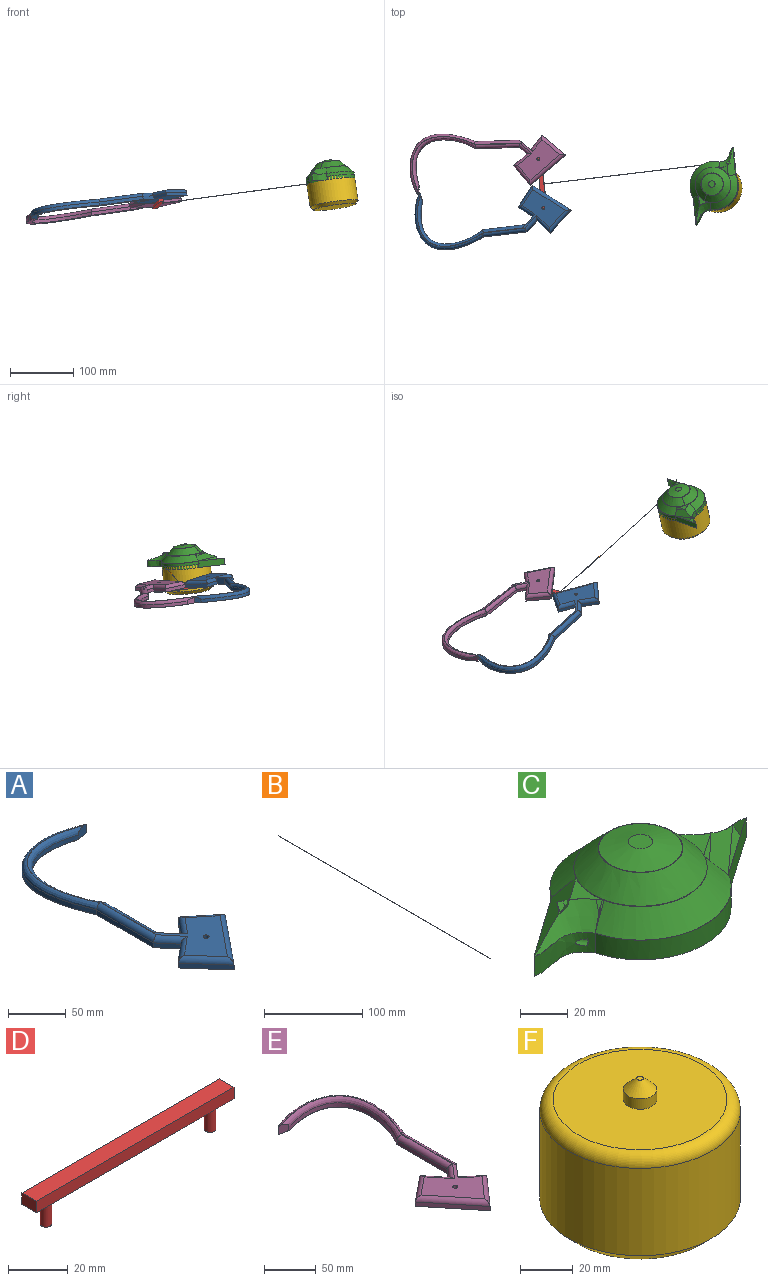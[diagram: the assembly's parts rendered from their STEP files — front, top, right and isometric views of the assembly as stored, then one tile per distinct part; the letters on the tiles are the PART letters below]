
ASSEMBLY  parts=6 mates=5
PART A: 83 faces, bbox 104.8x247.4x10.2 mm
  f0: plane 11.82x8.9mm, normal (0.47,0.88,0), area 103.2mm2, adj f41,f42,f52,f53
  f1: extruded ~105.07x82.64mm, area 859.2mm2, adj f21,f31,f42,f43
  f2: plane 69.4x5.06mm, normal (-1,0,0), area 350.9mm2, adj f24,f26,f31,f32
  f3: plane 18.2x15.29mm, normal (-0.77,-0.64,0), area 120.2mm2, adj f23,f26,f29,f30
  f4: plane 21.75x18.27mm, normal (-0.64,0.77,0), area 143.6mm2, adj f20,f30,f38,f39
  f5: plane 36.29x32.08mm, normal (-0.75,-0.66,0), area 244.9mm2, adj f6,f18,f39,f49
  f6: plane 56.58x45.93mm, normal (0.78,-0.63,0), area 368.5mm2, adj f5,f17,f54,f55
  f7: plane 31.62x25.67mm, normal (0.63,0.78,0), area 205.9mm2, adj f16,f55,f62,f63
  f8: plane 22.05x17.9mm, normal (-0.78,0.63,0), area 143.6mm2, adj f15,f63,f69,f70
  f9: plane 20.99x18.36mm, normal (0.75,0.66,0), area 182.8mm2, adj f70,f73,f75,f78,f79,f81
  f10: plane 69.4x5.06mm, normal (1,0,0), area 350.9mm2, adj f19,f67,f74,f79
  f11: extruded ~96.07x73.17mm, area 789mm2, adj f22,f60,f67,f68
  f12: plane 12.44x9.99mm, normal (0.2,-0.98,0), area 114.1mm2, adj f46,f52,f56,f60,f61
  f13: plane 134.23x63.66mm, normal (0,0,1), area 2042.7mm2, adj f15,f16,f17,f18,f19,f20,f22,f23
  f14: plane 247.28x94.44mm, normal (0,0,-1), area 5354.1mm2, adj f29,f32,f33,f37,f38,f43,f49,f53
  f15: cylinder r=5.08mm len=25.93mm, axis (0.63,0.78,0), area 209.9mm2, adj f8,f13,f59,f73
  f16: cylinder r=5.08mm len=34.83mm, axis (0.78,-0.63,0), area 284.7mm2, adj f7,f13,f50,f59
  f17: cylinder r=5.08mm len=59.79mm, axis (-0.63,-0.78,0), area 537.5mm2, adj f6,f13,f18,f50
  f18: cylinder r=5.08mm len=39.66mm, axis (-0.66,0.75,0), area 341.9mm2, adj f5,f13,f17,f34
  f19: cylinder r=5.08mm len=69.4mm, axis (0,-1,0), area 524.7mm2, adj f10,f13,f64,f81
  f20: cylinder r=5.08mm len=28.92mm, axis (0.77,0.64,0), area 226.3mm2, adj f4,f13,f27,f34
  f21: bspline ~106.69x102.31mm, area 1272.1mm2, adj f1,f36,f41,f45,f46
  f22: bspline ~104.81x101.02mm, area 1186.2mm2, adj f11,f13,f35,f40,f45,f56,f64
  f23: cylinder r=5.08mm len=25.37mm, axis (-0.64,0.77,0), area 202.7mm2, adj f3,f13,f25,f27
  f24: cylinder r=5.08mm len=70.38mm, axis (0,1,0), area 550.3mm2, adj f2,f13,f25,f35,f36
  f25: bspline ~5.74x5.08mm, area 0.1mm2, adj f23,f24,f26
  f26: cylinder r=0.02mm len=5.06mm, axis (0,0,-1), area 0.1mm2, adj f2,f3,f25,f28
  f27: bspline ~7.18x5.25mm, area 0.1mm2, adj f20,f23,f30
  f28: sphere r=0.02mm, area 0mm2, adj f26,f29,f32
  f29: cylinder r=0.02mm len=18.21mm, axis (0.64,-0.77,0), area 0.9mm2, adj f3,f14,f28,f33
  f30: cylinder r=0.02mm len=5.06mm, axis (0,0,1), area 0.2mm2, adj f3,f4,f27,f33
  f31: cylinder r=0.02mm len=5.06mm, axis (0,0,-1), area 0mm2, adj f1,f2,f36,f37
  f32: cylinder r=0.02mm len=69.4mm, axis (0,-1,0), area 2.6mm2, adj f2,f14,f28,f37
  f33: torus R=0.05mm, axis (0,0,1), area 0mm2, adj f14,f29,f30,f38
  f34: bspline ~7.26x5.75mm, area 0.1mm2, adj f18,f20,f39
  f35: bspline ~3.85x1.02mm, area 0mm2, adj f22,f24,f40
  f36: bspline ~5.38x5.07mm, area 0mm2, adj f21,f24,f31,f40
  f37: torus R=0.05mm, axis (0,0,1), area 0mm2, adj f14,f31,f32,f43
  f38: cylinder r=0.02mm len=21.76mm, axis (-0.77,-0.64,0), area 1.1mm2, adj f4,f14,f33,f44
  f39: cylinder r=0.02mm len=5.06mm, axis (0,0,1), area 0.2mm2, adj f4,f5,f34,f44
  f40: bspline ~0x0mm, area 0mm2, adj f22,f35,f36,f45
  f41: bspline ~13.83x7.29mm, area 0.2mm2, adj f0,f21,f42,f47
  f42: cylinder r=0.02mm len=5.06mm, axis (0,0,-1), area 0mm2, adj f0,f1,f41,f48
  f43: bspline ~107.3x83.54mm, area 6.4mm2, adj f1,f14,f37,f48
  f44: sphere r=0.02mm, area 0mm2, adj f38,f39,f49
  f45: bspline ~102x94.69mm, area 1.1mm2, adj f21,f22,f40,f51
  f46: bspline ~5.31x1.41mm, area 0.2mm2, adj f12,f21,f47,f51
  f47: sphere r=0.02mm, area 0mm2, adj f41,f46,f52
  f48: sphere r=0.02mm, area 0mm2, adj f42,f43,f53
  f49: cylinder r=0.02mm len=36.31mm, axis (0.66,-0.75,0), area 1.8mm2, adj f5,f14,f44,f54
  f50: bspline ~7.15x5.75mm, area 0.1mm2, adj f16,f17,f55
  f51: sphere r=0.02mm, area 0mm2, adj f45,f46,f56
  f52: cylinder r=0.02mm len=8.9mm, axis (0,0,-1), area 0.5mm2, adj f0,f12,f47,f57
  f53: cylinder r=0.02mm len=11.83mm, axis (-0.88,0.47,0), area 0.5mm2, adj f0,f14,f48,f57
  f54: cylinder r=0.02mm len=56.6mm, axis (0.63,0.78,0), area 2.8mm2, adj f6,f14,f49,f58
  f55: cylinder r=0.02mm len=5.06mm, axis (0,0,-1), area 0.2mm2, adj f6,f7,f50,f58
  f56: bspline ~9.92x5.18mm, area 0.2mm2, adj f12,f22,f51,f60
  f57: sphere r=0.02mm, area 0mm2, adj f52,f53,f61
  f58: sphere r=0.02mm, area 0mm2, adj f54,f55,f62
  f59: bspline ~7.15x5.75mm, area 0.1mm2, adj f15,f16,f63
  f60: cylinder r=0.02mm len=5.06mm, axis (0,0,-1), area 0.1mm2, adj f11,f12,f56,f65
  f61: cylinder r=0.02mm len=12.44mm, axis (0.98,0.2,0), area 0.5mm2, adj f12,f14,f57,f65
  f62: cylinder r=0.02mm len=31.64mm, axis (-0.78,0.63,0), area 1.5mm2, adj f7,f14,f58,f66
  f63: cylinder r=0.02mm len=5.06mm, axis (0,0,-1), area 0.2mm2, adj f7,f8,f59,f66
  f64: bspline ~5.4x5.08mm, area 0mm2, adj f19,f22,f67
  f65: sphere r=0.02mm, area 0mm2, adj f60,f61,f68
  f66: sphere r=0.02mm, area 0mm2, adj f62,f63,f69
  f67: cylinder r=0.02mm len=5.06mm, axis (0,0,-1), area 0.1mm2, adj f10,f11,f64,f71
  f68: bspline ~97.25x73.52mm, area 5.9mm2, adj f11,f14,f65,f71
  f69: cylinder r=0.02mm len=22.06mm, axis (-0.63,-0.78,0), area 1.1mm2, adj f8,f14,f66,f72
  f70: cylinder r=0.02mm len=5.06mm, axis (0,0,-1), area 0.2mm2, adj f8,f9,f72,f73
  f71: sphere r=0.02mm, area 0mm2, adj f67,f68,f74
  f72: torus R=0.05mm, axis (0,0,1), area 0mm2, adj f14,f69,f70,f75
  f73: bspline ~5.1x3.9mm, area 0.3mm2, adj f9,f15,f70,f76
  f74: cylinder r=0.02mm len=69.4mm, axis (0,1,0), area 2.6mm2, adj f10,f14,f71,f77
  f75: cylinder r=0.02mm len=12.61mm, axis (-0.66,0.75,0), area 0.6mm2, adj f9,f14,f72,f77
  f76: bspline ~0.52x0.5mm, area 0mm2, adj f13,f73,f78
  f77: torus R=0.05mm, axis (0,0,1), area 0mm2, adj f14,f74,f75,f79
  f78: cylinder r=0.02mm len=21mm, axis (0.66,-0.75,0), area 1.1mm2, adj f9,f13,f76,f80
  f79: cylinder r=0.02mm len=5.06mm, axis (0,0,-1), area 0.1mm2, adj f9,f10,f77,f81
  f80: bspline ~0.85x0.7mm, area 0mm2, adj f13,f78,f81
  f81: bspline ~6.86x5.99mm, area 0.2mm2, adj f9,f19,f79,f80
  f82: cylinder r=2.54mm len=10.16mm, axis (0,0,1), area 162.1mm2, adj f13,f14
PART B: 3 faces, bbox 0.3x304.8x0.3 mm
  f0: cylinder r=0.13mm len=304.8mm, axis (0,1,0), area 243.2mm2, adj f1,f2
  f1: plane 0.25x0.25mm, normal (0,-1,0), area 0.1mm2, adj f0
  f2: plane 0.25x0.25mm, normal (0,1,0), area 0.1mm2, adj f0
PART C: 27 faces, bbox 134.7x76.8x34.3 mm
  f0: extruded ~30.19x10.16mm, area 328.9mm2, adj f3,f4,f8,f11,f25,f26
  f1: plane 19.93x13.42mm, normal (0,0,1), area 82.2mm2, adj f9,f11,f19
  f2: plane 21.28x13.84mm, normal (0,0,1), area 96.7mm2, adj f12,f14,f19
  f3: plane 35.52x25.08mm, normal (-0.58,0.82,0), area 430.4mm2, adj f0,f7,f8,f9,f26
  f4: cylinder r=38.1mm len=69.58mm, axis (0,0,-1), area 907.9mm2, adj f0,f5,f8,f13
  f5: plane 34.68x24.14mm, normal (0.57,-0.82,0), area 429.3mm2, adj f4,f6,f8,f14
  f6: extruded ~31.93x10.16mm, area 358.3mm2, adj f5,f7,f8,f12
  f7: cylinder r=38.1mm len=67.01mm, axis (0,0,-1), area 841.3mm2, adj f3,f6,f8,f10
  f8: plane 134.45x76.2mm, normal (0,0,-1), area 3218.9mm2, adj f0,f3,f4,f5,f6,f7,f16
  f9: bspline ~43x34.53mm, area 401.9mm2, adj f1,f3,f10,f11,f18
  f10: bspline ~71.23x30.18mm, area 1054.3mm2, adj f7,f9,f12,f18
  f11: bspline ~39.65x19.5mm, area 321.3mm2, adj f0,f1,f9,f13,f21
  f12: bspline ~41.04x20.22mm, area 368mm2, adj f2,f6,f10,f14,f18
  f13: bspline ~72.78x36.07mm, area 1142.7mm2, adj f4,f11,f14,f21
  f14: bspline ~42.48x33.87mm, area 408.7mm2, adj f2,f5,f12,f13,f21
  f15: cone r=0mm half-angle=59deg, axis (0,0,-1), area 1312.1mm2, adj f16,f17
  f16: cylinder r=25.4mm len=50.8mm, axis (0,0,-1), area 2432.2mm2, adj f8,f15
  f17: plane 33.89x33.89mm, normal (0,0,-1), area 902.1mm2, adj f15
  f18: plane 50.82x19.25mm, normal (0,0,-1), area 6.1mm2, adj f9,f10,f12,f19
  f19: cylinder r=28.04mm len=56.07mm, axis (0,0,-1), area 44.7mm2, adj f1,f2,f18,f21,f22
  f20: plane 35.77x35.77mm, normal (0,0,1), area 24.6mm2, adj f22,f24
  f21: plane 52.69x22.63mm, normal (0,0,-1), area 6.6mm2, adj f11,f13,f14,f19
  f22: bspline ~56.07x56.07mm, area 2075.9mm2, adj f19,f20
  f23: plane 10.26x10.26mm, normal (0,0,1), area 82.7mm2, adj f24
  f24: bspline ~35.31x35.31mm, area 926.9mm2, adj f20,f23
  f25: cone r=0mm half-angle=59deg, axis (-0.58,0.82,0), area 10.9mm2, adj f0,f26
  f26: cylinder r=1.91mm len=17.76mm, axis (-0.58,0.82,0), area 217.9mm2, adj f0,f3,f25
PART D: 10 faces, bbox 93.7x6.9x15 mm
  f0: plane 93.74x4.8mm, normal (0,1,0), area 449.8mm2, adj f1,f3,f4,f5
  f1: plane 93.74x6.91mm, normal (0,0,1), area 648mm2, adj f0,f2,f4,f5
  f2: plane 93.74x4.8mm, normal (0,-1,0), area 449.8mm2, adj f1,f3,f4,f5
  f3: plane 93.74x6.91mm, normal (0,0,-1), area 623.3mm2, adj f0,f2,f4,f5,f6,f8
  f4: plane 6.91x4.8mm, normal (1,0,0), area 33.2mm2, adj f0,f1,f2,f3
  f5: plane 6.91x4.8mm, normal (-1,0,0), area 33.2mm2, adj f0,f1,f2,f3
  f6: cylinder r=1.98mm len=10.16mm, axis (0,0,1), area 126.5mm2, adj f3,f7
  f7: plane 3.96x3.96mm, normal (0,0,-1), area 12.3mm2, adj f6
  f8: cylinder r=1.98mm len=10.16mm, axis (0,0,1), area 126.5mm2, adj f3,f9
  f9: plane 3.96x3.96mm, normal (0,0,-1), area 12.3mm2, adj f8
PART E: 82 faces, bbox 104.8x247.3x10.6 mm
  f0: extruded ~96.07x73.17mm, area 789mm2, adj f24,f26,f31,f32
  f1: plane 69.4x5.06mm, normal (-1,0,0), area 350.9mm2, adj f23,f26,f29,f30
  f2: plane 12.59x11.02mm, normal (-0.75,0.66,0), area 84.6mm2, adj f20,f30,f38,f39
  f3: plane 22.05x17.9mm, normal (0.78,0.63,0), area 143.6mm2, adj f19,f39,f50,f51
  f4: plane 31.62x25.67mm, normal (-0.63,0.78,0), area 205.9mm2, adj f18,f51,f59,f60
  f5: plane 56.58x45.93mm, normal (-0.78,-0.63,0), area 368.5mm2, adj f6,f17,f60,f65
  f6: plane 36.29x32.08mm, normal (0.75,-0.66,0), area 244.9mm2, adj f5,f16,f68,f69
  f7: plane 21.75x18.27mm, normal (0.64,0.77,0), area 143.6mm2, adj f15,f69,f75,f79
  f8: plane 21.57x18.12mm, normal (0.77,-0.64,0), area 237.2mm2, adj f70,f73,f74,f76,f79,f80
  f9: plane 69.4x5.06mm, normal (1,0,0), area 350.9mm2, adj f22,f61,f67,f70
  f10: extruded ~105.07x82.64mm, area 859.2mm2, adj f21,f53,f61,f62
  f11: plane 11.82x8.9mm, normal (-0.47,0.88,0), area 103.2mm2, adj f42,f48,f53,f54
  f12: plane 12.44x9.99mm, normal (-0.2,-0.98,0), area 114.1mm2, adj f31,f35,f36,f42,f43
  f13: plane 134.22x63.64mm, normal (0,0,1), area 2026.8mm2, adj f15,f16,f17,f18,f19,f20,f22,f23
  f14: plane 247.28x94.44mm, normal (0,0,-1), area 5355.2mm2, adj f29,f32,f33,f38,f43,f44,f50,f54
  f15: cylinder r=5.08mm len=25.01mm, axis (0.77,-0.64,0), area 205.9mm2, adj f7,f13,f66,f80
  f16: cylinder r=5.08mm len=39.66mm, axis (-0.66,-0.75,0), area 341.9mm2, adj f6,f13,f17,f66
  f17: cylinder r=5.08mm len=59.79mm, axis (-0.63,0.78,0), area 537.5mm2, adj f5,f13,f16,f56
  f18: cylinder r=5.08mm len=34.83mm, axis (0.78,0.63,0), area 284.7mm2, adj f4,f13,f45,f56
  f19: cylinder r=5.08mm len=29.95mm, axis (0.63,-0.78,0), area 230.6mm2, adj f3,f13,f34,f45
  f20: cylinder r=5.08mm len=21.94mm, axis (0.66,0.75,0), area 165.3mm2, adj f2,f13,f27,f34
  f21: bspline ~106.69x102.31mm, area 1272.1mm2, adj f10,f36,f47,f48,f57
  f22: cylinder r=5.08mm len=76.4mm, axis (0,-1,0), area 575.1mm2, adj f9,f13,f46,f57,f73
  f23: cylinder r=5.08mm len=71.31mm, axis (0,1,0), area 555.6mm2, adj f1,f13,f25,f27
  f24: bspline ~104.81x101.02mm, area 1186.2mm2, adj f0,f13,f25,f35,f46,f47,f52
  f25: bspline ~5.4x5.08mm, area 0mm2, adj f23,f24,f26
  f26: cylinder r=0.02mm len=5.06mm, axis (0,0,-1), area 0.1mm2, adj f0,f1,f25,f28
  f27: bspline ~5.25x5.09mm, area 0.1mm2, adj f20,f23,f30
  f28: sphere r=0.02mm, area 0mm2, adj f26,f29,f32
  f29: cylinder r=0.02mm len=69.4mm, axis (0,-1,0), area 2.6mm2, adj f1,f14,f28,f33
  f30: cylinder r=0.02mm len=5.06mm, axis (0,0,-1), area 0.1mm2, adj f1,f2,f27,f33
  f31: cylinder r=0.02mm len=5.06mm, axis (0,0,-1), area 0.1mm2, adj f0,f12,f35,f37
  f32: bspline ~97.25x73.52mm, area 5.9mm2, adj f0,f14,f28,f37
  f33: torus R=0.05mm, axis (0,0,1), area 0mm2, adj f14,f29,f30,f38
  f34: bspline ~7.9x5.25mm, area 0.1mm2, adj f19,f20,f39
  f35: bspline ~9.92x5.18mm, area 0.2mm2, adj f12,f24,f31,f40
  f36: bspline ~5.31x1.41mm, area 0.2mm2, adj f12,f21,f40,f41
  f37: sphere r=0.02mm, area 0mm2, adj f31,f32,f43
  f38: cylinder r=0.02mm len=12.61mm, axis (-0.66,-0.75,0), area 0.6mm2, adj f2,f14,f33,f44
  f39: cylinder r=0.02mm len=5.06mm, axis (0,0,-1), area 0.2mm2, adj f2,f3,f34,f44
  f40: sphere r=0.02mm, area 0mm2, adj f35,f36,f47
  f41: sphere r=0.02mm, area 0mm2, adj f36,f42,f48
  f42: cylinder r=0.02mm len=8.9mm, axis (0,0,-1), area 0.5mm2, adj f11,f12,f41,f49
  f43: cylinder r=0.02mm len=12.44mm, axis (0.98,-0.2,0), area 0.5mm2, adj f12,f14,f37,f49
  f44: torus R=0.05mm, axis (0,0,1), area 0mm2, adj f14,f38,f39,f50
  f45: bspline ~7.15x5.75mm, area 0.1mm2, adj f18,f19,f51
  f46: bspline ~3.85x1.02mm, area 0mm2, adj f22,f24,f52
  f47: bspline ~102x94.69mm, area 1.1mm2, adj f21,f24,f40,f52
  f48: bspline ~13.83x7.29mm, area 0.2mm2, adj f11,f21,f41,f53
  f49: sphere r=0.02mm, area 0mm2, adj f42,f43,f54
  f50: cylinder r=0.02mm len=22.06mm, axis (-0.63,0.78,0), area 1.1mm2, adj f3,f14,f44,f55
  f51: cylinder r=0.02mm len=5.06mm, axis (0,0,-1), area 0.2mm2, adj f3,f4,f45,f55
  f52: bspline ~0x0mm, area 0mm2, adj f24,f46,f47,f57
  f53: cylinder r=0.02mm len=5.06mm, axis (0,0,-1), area 0mm2, adj f10,f11,f48,f58
  f54: cylinder r=0.02mm len=11.83mm, axis (-0.88,-0.47,0), area 0.5mm2, adj f11,f14,f49,f58
  f55: sphere r=0.02mm, area 0mm2, adj f50,f51,f59
  f56: bspline ~7.15x5.75mm, area 0.1mm2, adj f17,f18,f60
  f57: bspline ~5.38x5.07mm, area 0mm2, adj f21,f22,f52,f61
  f58: sphere r=0.02mm, area 0mm2, adj f53,f54,f62
  f59: cylinder r=0.02mm len=31.64mm, axis (-0.78,-0.63,0), area 1.5mm2, adj f4,f14,f55,f63
  f60: cylinder r=0.02mm len=5.06mm, axis (0,0,-1), area 0.2mm2, adj f4,f5,f56,f63
  f61: cylinder r=0.02mm len=5.06mm, axis (0,0,-1), area 0mm2, adj f9,f10,f57,f64
  f62: bspline ~107.3x83.54mm, area 6.4mm2, adj f10,f14,f58,f64
  f63: sphere r=0.02mm, area 0mm2, adj f59,f60,f65
  f64: torus R=0.05mm, axis (0,0,1), area 0mm2, adj f14,f61,f62,f67
  f65: cylinder r=0.02mm len=56.6mm, axis (0.63,-0.78,0), area 2.8mm2, adj f5,f14,f63,f68
  f66: bspline ~7.26x5.75mm, area 0.1mm2, adj f15,f16,f69
  f67: cylinder r=0.02mm len=69.4mm, axis (0,1,0), area 2.6mm2, adj f9,f14,f64,f71
  f68: cylinder r=0.02mm len=36.31mm, axis (0.66,0.75,0), area 1.8mm2, adj f6,f14,f65,f72
  f69: cylinder r=0.02mm len=5.06mm, axis (0,0,1), area 0.2mm2, adj f6,f7,f66,f72
  f70: cylinder r=0.02mm len=5.06mm, axis (0,0,-1), area 0.1mm2, adj f8,f9,f71,f73
  f71: sphere r=0.02mm, area 0mm2, adj f67,f70,f74
  f72: sphere r=0.02mm, area 0mm2, adj f68,f69,f75
  f73: bspline ~7.08x5.96mm, area 0.3mm2, adj f8,f22,f70,f76
  f74: cylinder r=0.02mm len=18.21mm, axis (0.64,0.77,0), area 0.9mm2, adj f8,f14,f71,f77
  f75: cylinder r=0.02mm len=21.76mm, axis (-0.77,0.64,0), area 1.1mm2, adj f7,f14,f72,f77
  f76: cylinder r=0.02mm len=15.57mm, axis (-0.64,-0.77,0), area 0.8mm2, adj f8,f13,f73,f78
  f77: torus R=0.05mm, axis (0,0,1), area 0mm2, adj f14,f74,f75,f79
  f78: bspline ~0.62x0.48mm, area 0mm2, adj f13,f76,f80
  f79: cylinder r=0.02mm len=5.06mm, axis (0,0,1), area 0.2mm2, adj f7,f8,f77,f80
  f80: torus R=5.1mm, axis (0.77,-0.64,0), area 0.3mm2, adj f8,f15,f78,f79
  f81: cylinder r=2.54mm len=10.16mm, axis (0,0,1), area 162.1mm2, adj f13,f14
PART F: 8 faces, bbox 82.5x82.5x60.7 mm
  f0: cylinder r=38.1mm len=76.2mm, axis (0,0,1), area 9728.8mm2, adj f3,f4
  f1: plane 66.04x66.04mm, normal (0,0,-1), area 3425.3mm2, adj f4
  f2: plane 66.04x66.04mm, normal (0,0,1), area 3298.7mm2, adj f3,f5
  f3: torus R=33.02mm, axis (0,0,1), area 1817.7mm2, adj f0,f2
  f4: cone r=38.1mm half-angle=45deg, axis (0,0,1), area 1605.2mm2, adj f0,f1
  f5: cylinder r=6.35mm len=12.7mm, axis (0,0,-1), area 192.5mm2, adj f2,f7
  f6: plane 2.54x2.54mm, normal (0,0,1), area 5.1mm2, adj f7
  f7: cone r=1.27mm half-angle=45deg, axis (0,0,-1), area 172mm2, adj f5,f6
PLACE A rot(axis=(-0.12,-0.01,0.99),96.7deg) t=(-583.35,-938.28,-63.78)mm
PLACE B rot(axis=(0.02,-0.13,-0.99),84.1deg) t=(-179.06,-909.22,-10.76)mm
PLACE C rot(axis=(0.04,-0.09,-0.99),119.1deg) t=(-209.88,-948.57,-16.39)mm
PLACE D rot(axis=(-0.74,0.66,-0.09),178.8deg) t=(-482.55,-945.32,-50.94)mm
PLACE E rot(axis=(-0.12,-0.02,0.99),91.8deg) t=(-584.97,-969.6,-60.85)mm
PLACE F rot(axis=(-0.57,-0.82,0),10deg) t=(-211.36,-947.53,-6.13)mm
MATE fastened B.f0 <-> C.f25  axis (0.98,0.12,0.13) through (-179.06,-909.22,-10.76)mm
MATE fastened B.f0 <-> D.f2  axis (-0.98,-0.12,-0.13) through (-479.14,-944.92,-50.49)mm
MATE revolute C.f15 <-> F.f5  axis (0.14,-0.1,-0.98) through (-212.77,-946.55,3.62)mm
MATE revolute A.f82 <-> D.f8  axis (-0.14,0.1,0.98) through (-480.34,-982.59,-34.1)mm
MATE revolute E.f81 <-> D.f6  axis (-0.14,0.1,0.98) through (-488.32,-905.56,-43.05)mm
